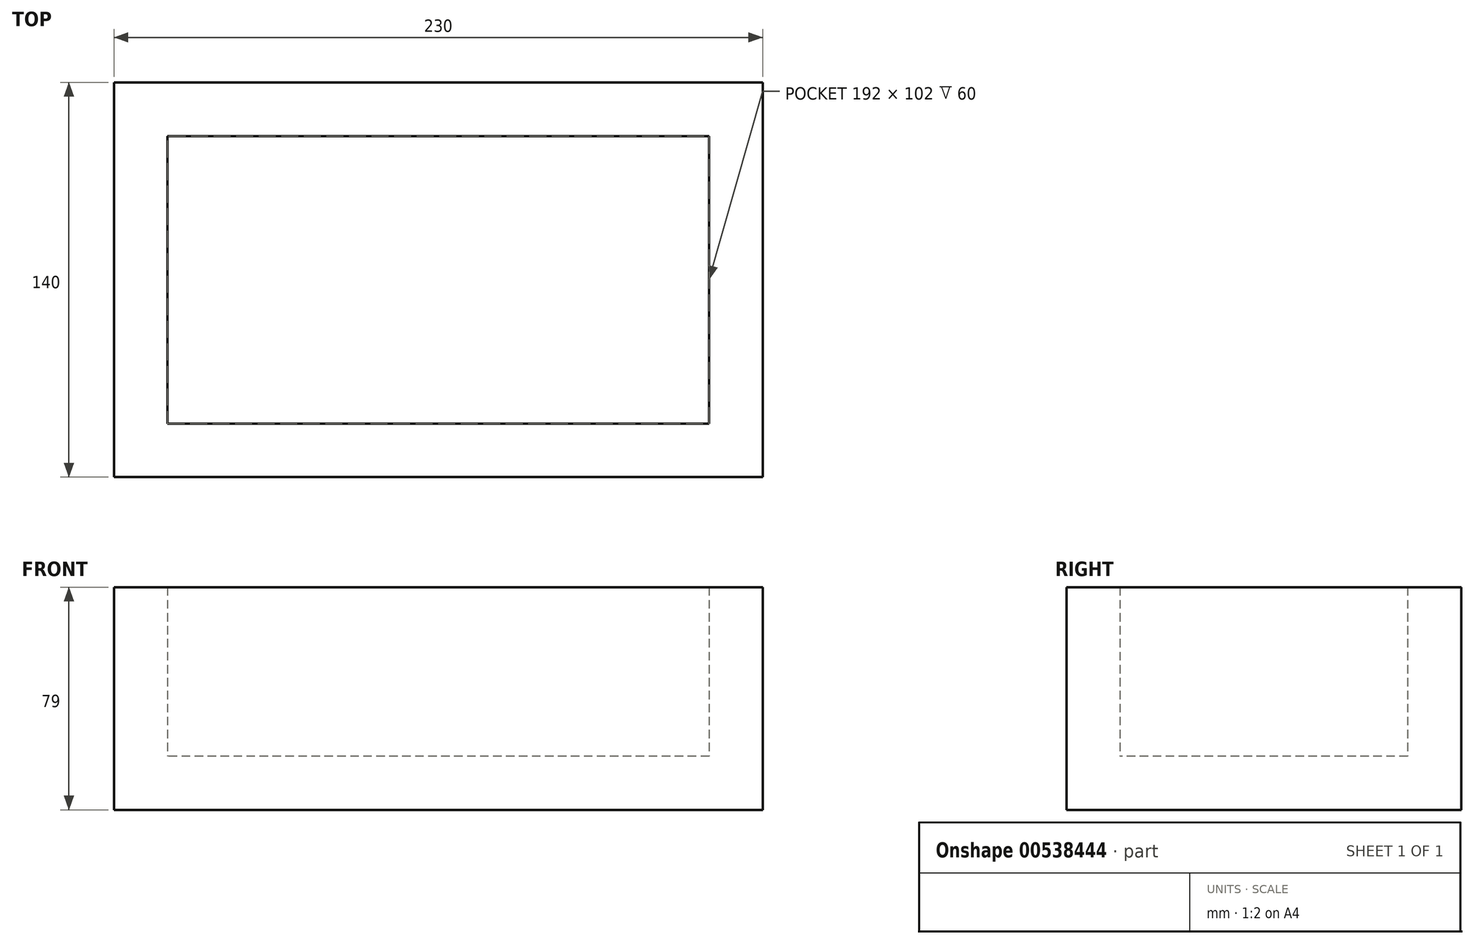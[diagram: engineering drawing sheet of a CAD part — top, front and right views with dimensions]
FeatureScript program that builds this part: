
annotation { "Feature Type Name" : "Feature", "Feature Type Description" : "" }
export const myFeature = defineFeature(function(context is Context, id is Id, definition is map)
    precondition{}
    {
        {
            var Q0;
            Q0=qCreatedBy(makeId("Top.planeOp"),FACE);
            var sketch = newSketch(context, id + "F0", { "sketchPlane" : qUnion([Q0])});
            skLineSegment(sketch, "E0.bottom", {"start": v(115, -70) * mm, "end": v(-115, -70) * mm});
            skLineSegment(sketch, "E0.top", {"start": v(115, 70) * mm, "end": v(-115, 70) * mm});
            skLineSegment(sketch, "E0.left", {"start": v(115, -70) * mm, "end": v(115, 70) * mm});
            skLineSegment(sketch, "E0.right", {"start": v(-115, -70) * mm, "end": v(-115, 70) * mm});
            skPoint(sketch, "E0.middle", {"position": v(0, 0) * mm});
            skSolve(sketch);
        }
        {
            var Q0;
            Q0=makeQuery(id+"F0.imprint","IMPRINT",FACE,{"disambiguationData":[TD([[makeQuery(id+"F0.imprint","IMPRINT",EDGE,{"derivedFrom":sQuery(id+"F0.wireOp",EDGE,"E0.bottom")}),-1.0]])]});
            extrude(context, id + "F1", {"entities" : qUnion([Q0]), "depth" : 19 * mm, "offsetDistance" : 25 * mm});
        }
        {
            var Q0;
            Q0=makeQuery(id+"F1.opExtrude","CAP_FACE",FACE,{"disambiguationData":[OSD([sQuery(id+"F0.wireOp",EDGE,"E0.bottom"),sQuery(id+"F0.wireOp",EDGE,"E0.top"),sQuery(id+"F0.wireOp",EDGE,"E0.left"),sQuery(id+"F0.wireOp",EDGE,"E0.right")])],"isStart":false});
            var sketch = newSketch(context, id + "F2", { "sketchPlane" : qUnion([Q0])});
            skLineSegment(sketch, "E1.bottom", {"start": v(115, 70) * mm, "end": v(-115, 70) * mm});
            skLineSegment(sketch, "E1.top", {"start": v(115, -70) * mm, "end": v(-115, -70) * mm});
            skLineSegment(sketch, "E1.left", {"start": v(115, 70) * mm, "end": v(115, -70) * mm});
            skLineSegment(sketch, "E1.right", {"start": v(-115, 70) * mm, "end": v(-115, -70) * mm});
            skSolve(sketch);
        }
        {
            var Q0;
            Q0=makeQuery(id+"F2.imprint","IMPRINT",FACE,{"disambiguationData":[TD([[makeQuery(id+"F2.imprint","IMPRINT",EDGE,{"derivedFrom":sQuery(id+"F2.wireOp",EDGE,"E1.bottom")}),1.0]])]});
            var sketch = newSketch(context, id + "F3", { "sketchPlane" : qUnion([Q0])});
            skLineSegment(sketch, "E2.bottom", {"start": v(96, 51) * mm, "end": v(-96, 51) * mm});
            skLineSegment(sketch, "E2.top", {"start": v(96, -51) * mm, "end": v(-96, -51) * mm});
            skLineSegment(sketch, "E2.left", {"start": v(96, 51) * mm, "end": v(96, -51) * mm});
            skLineSegment(sketch, "E2.right", {"start": v(-96, 51) * mm, "end": v(-96, -51) * mm});
            skPoint(sketch, "E2.middle", {"position": v(0, 0) * mm});
            skSolve(sketch);
        }
        {
            var Q0;
            Q0=makeQuery(id+"F3.imprint","IMPRINT",FACE,{"disambiguationData":[TD([[makeQuery(id+"F3.imprint","IMPRINT",EDGE,{"derivedFrom":sQuery(id+"F3.wireOp",EDGE,"E2.bottom")}),-1.0]])]});
            extrude(context, id + "F4", {"entities" : qUnion([Q0]), "operationType" : NewBodyOperationType.ADD, "depth" : 60 * mm, "offsetDistance" : 25 * mm});
        }
    });
